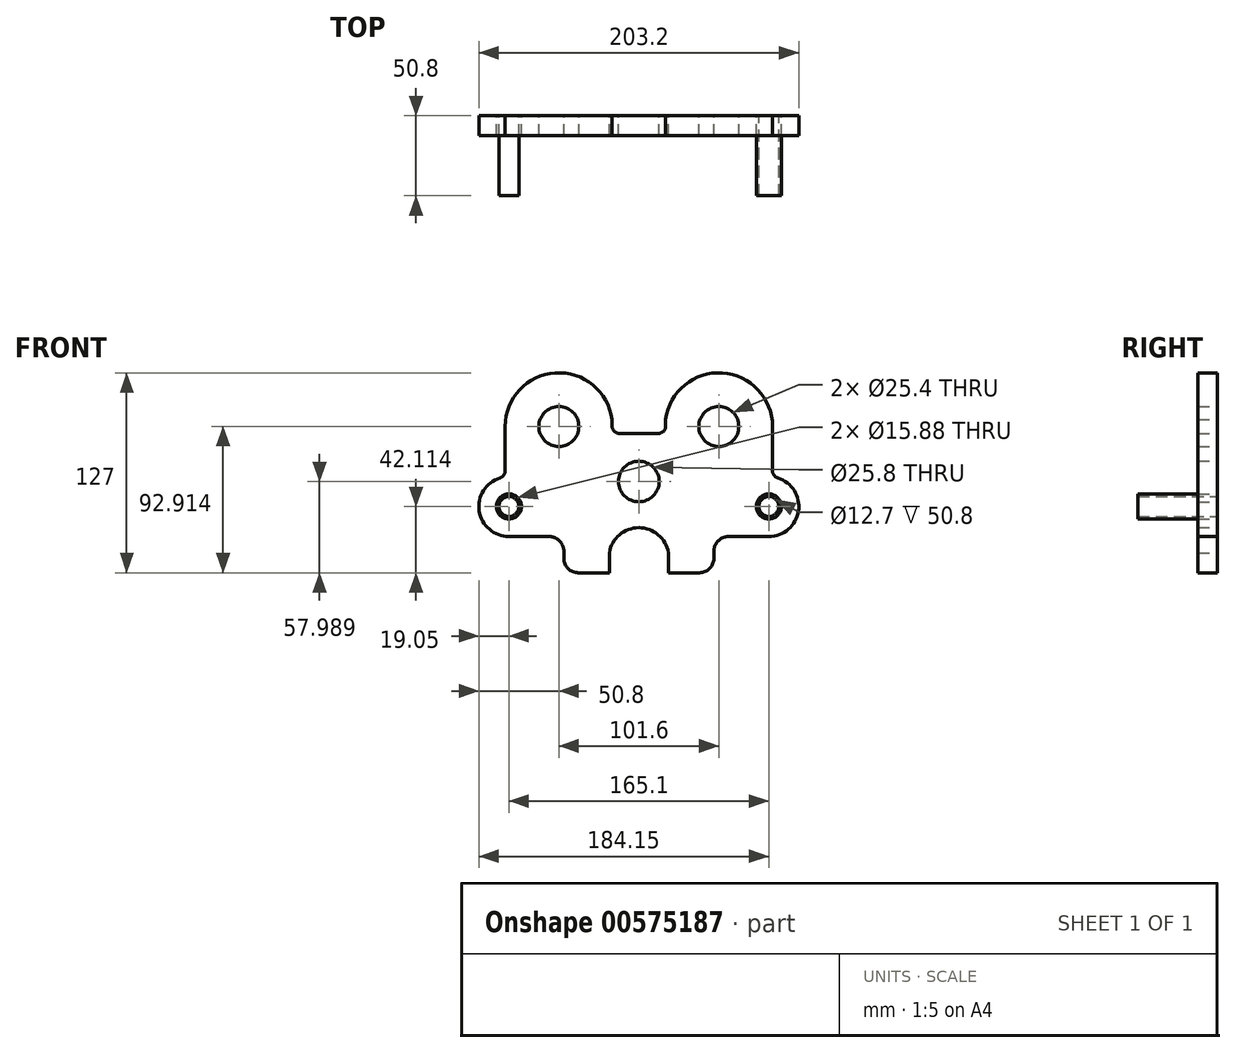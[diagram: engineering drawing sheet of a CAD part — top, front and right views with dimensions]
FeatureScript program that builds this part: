
annotation { "Feature Type Name" : "Feature", "Feature Type Description" : "" }
export const myFeature = defineFeature(function(context is Context, id is Id, definition is map)
    precondition{}
    {
        {
            var Q0;
            Q0=qCreatedBy(makeId("Front.planeOp"),FACE);
            var sketch = newSketch(context, id + "F0", { "sketchPlane" : qUnion([Q0])});
            skArc(sketch, "E0.MirrorCS", {"start": v(17, 52.22) * mm, "mid": v(53.03, 81.78) * mm, "end": v(84.89, 47.76) * mm});
            skLineSegment(sketch, "E1", {"start": v(84.89, 47.76) * mm, "end": v(84.89, 19.7) * mm});
            skCircle(sketch, "E2", {"center": v(50.8, 47.76) * mm, "radius": 12.7 * mm});
            skLineSegment(sketch, "E3", {"start": v(47.62, -31.6) * mm, "end": v(47.62, -36.03) * mm});
            skLineSegment(sketch, "E4", {"start": v(57.15, -22.08) * mm, "end": v(82.55, -22.09) * mm});
            skLineSegment(sketch, "E5", {"start": v(38.5, -45.15) * mm, "end": v(18.8, -45.15) * mm});
            skLineSegment(sketch, "E6", {"start": v(0, 82.43) * mm, "end": v(0, -73.32) * mm, "construction": true});
            skArc(sketch, "E7", {"start": v(82.55, -22.09) * mm, "mid": v(101.38, -5.92) * mm, "end": v(88.24, 15.14) * mm});
            skCircle(sketch, "E8", {"center": v(82.55, -3.04) * mm, "radius": 6.35 * mm});
            skCircle(sketch, "E9", {"center": v(0, 12.84) * mm, "radius": 12.9 * mm});
            skPoint(sketch, "E10.visualSharp", {"position": v(47.62, -22.08) * mm});
            skArc(sketch, "E10.filletArc", {"start": v(57.15, -22.08) * mm, "mid": v(50.4, -24.87) * mm, "end": v(47.62, -31.6) * mm});
            skPoint(sketch, "E11.visualSharp", {"position": v(47.62, -45.15) * mm});
            skArc(sketch, "E11.filletArc", {"start": v(38.5, -45.15) * mm, "mid": v(44.95, -42.48) * mm, "end": v(47.62, -36.03) * mm});
            skPoint(sketch, "E12.visualSharp", {"position": v(84.89, 15.87) * mm});
            skArc(sketch, "E12.filletArc", {"start": v(84.89, 19.7) * mm, "mid": v(85.82, 16.87) * mm, "end": v(88.24, 15.14) * mm});
            skLineSegment(sketch, "E13", {"start": v(-38.81, 12.84) * mm, "end": v(37.58, 12.82) * mm, "construction": true});
            skLineSegment(sketch, "E14", {"start": v(29.1, 47.76) * mm, "end": v(72.42, 47.76) * mm, "construction": true});
            skLineSegment(sketch, "E15", {"start": v(50.8, 71.2) * mm, "end": v(50.8, 24.74) * mm, "construction": true});
            skLineSegment(sketch, "E16", {"start": v(58.48, -3.04) * mm, "end": v(97.34, -3.04) * mm, "construction": true});
            skLineSegment(sketch, "E17", {"start": v(-27.2, -27.38) * mm, "end": v(26.4, -27.4) * mm, "construction": true});
            skLineSegment(sketch, "E18", {"start": v(82.55, 11.19) * mm, "end": v(82.55, -41.53) * mm, "construction": true});
            skLineSegment(sketch, "E19", {"start": v(17, 52.22) * mm, "end": v(17, 48.07) * mm});
            skLineSegment(sketch, "E20.MirrorCS", {"start": v(-17, 52.22) * mm, "end": v(-17, 48.07) * mm});
            skArc(sketch, "E21.MirrorCS", {"start": v(-17, 52.22) * mm, "mid": v(-53.03, 81.78) * mm, "end": v(-84.89, 47.76) * mm});
            skLineSegment(sketch, "E22.MirrorCS", {"start": v(-84.89, 47.76) * mm, "end": v(-84.89, 19.7) * mm});
            skArc(sketch, "E23.MirrorCS", {"start": v(-84.89, 19.7) * mm, "mid": v(-85.82, 16.87) * mm, "end": v(-88.24, 15.14) * mm});
            skArc(sketch, "E24.MirrorCS", {"start": v(-82.55, -22.09) * mm, "mid": v(-101.38, -5.92) * mm, "end": v(-88.24, 15.14) * mm});
            skLineSegment(sketch, "E25.MirrorCS", {"start": v(-57.15, -22.08) * mm, "end": v(-82.55, -22.09) * mm});
            skArc(sketch, "E26.MirrorCS", {"start": v(-57.15, -22.08) * mm, "mid": v(-50.4, -24.87) * mm, "end": v(-47.62, -31.6) * mm});
            skLineSegment(sketch, "E27.MirrorCS", {"start": v(-47.62, -31.6) * mm, "end": v(-47.62, -36.03) * mm});
            skArc(sketch, "E28.MirrorCS", {"start": v(-38.5, -45.15) * mm, "mid": v(-44.95, -42.48) * mm, "end": v(-47.62, -36.03) * mm});
            skLineSegment(sketch, "E29.MirrorCS", {"start": v(-38.5, -45.15) * mm, "end": v(-18.8, -45.15) * mm});
            skLineSegment(sketch, "E30", {"start": v(-12.23, 43.3) * mm, "end": v(12.23, 43.3) * mm});
            skLineSegment(sketch, "E31", {"start": v(-18.8, -45.15) * mm, "end": v(-18.8, -32.45) * mm});
            skLineSegment(sketch, "E32", {"start": v(18.8, -45.15) * mm, "end": v(18.8, -32.45) * mm});
            skArc(sketch, "E33", {"start": v(18.8, -32.45) * mm, "mid": v(0, -16.53) * mm, "end": v(-18.8, -32.45) * mm});
            skCircle(sketch, "E34.MirrorC", {"center": v(-50.8, 47.76) * mm, "radius": 12.7 * mm});
            skCircle(sketch, "E35.MirrorC", {"center": v(-82.55, -3.04) * mm, "radius": 6.35 * mm});
            skPoint(sketch, "E36.visualSharp", {"position": v(17, 43.3) * mm});
            skArc(sketch, "E36.filletArc", {"start": v(12.23, 43.3) * mm, "mid": v(15.6, 44.7) * mm, "end": v(17, 48.07) * mm});
            skPoint(sketch, "E37.visualSharp", {"position": v(-17, 43.3) * mm});
            skArc(sketch, "E37.filletArc", {"start": v(-17, 48.07) * mm, "mid": v(-15.6, 44.7) * mm, "end": v(-12.23, 43.3) * mm});
            skCircle(sketch, "E38", {"center": v(-82.55, -3.04) * mm, "radius": 7.94 * mm});
            skCircle(sketch, "E39", {"center": v(82.55, -3.04) * mm, "radius": 7.94 * mm});
            skSolve(sketch);
        }
        {
            var Q0;
            Q0=makeQuery(id+"F0.imprint","IMPRINT",FACE,{"disambiguationData":[TD([[makeQuery(id+"F0.imprint","IMPRINT",EDGE,{"derivedFrom":sQuery(id+"F0.wireOp",EDGE,"E8")}),-1.0]])]});
            extrude(context, id + "F1", {"entities" : qUnion([Q0]), "depth" : 50.8 * mm, "offsetDistance" : 25.4 * mm});
        }
        {
            var Q0;
            Q0=makeQuery(id+"F0.imprint","IMPRINT",FACE,{"disambiguationData":[TD([[makeQuery(id+"F0.imprint","IMPRINT",EDGE,{"derivedFrom":sQuery(id+"F0.wireOp",EDGE,"E35.MirrorC")}),1.0]])]});
            extrude(context, id + "F2", {"entities" : qUnion([Q0]), "depth" : 50.8 * mm, "offsetDistance" : 25.4 * mm});
        }
        {
            var Q0;
            Q0 = qSketchRegion(id + "F0", true);
            extrude(context, id + "F3", {"entities" : qUnion([Q0]), "depth" : 12.7 * mm, "offsetDistance" : 25.4 * mm});
        }
    });
